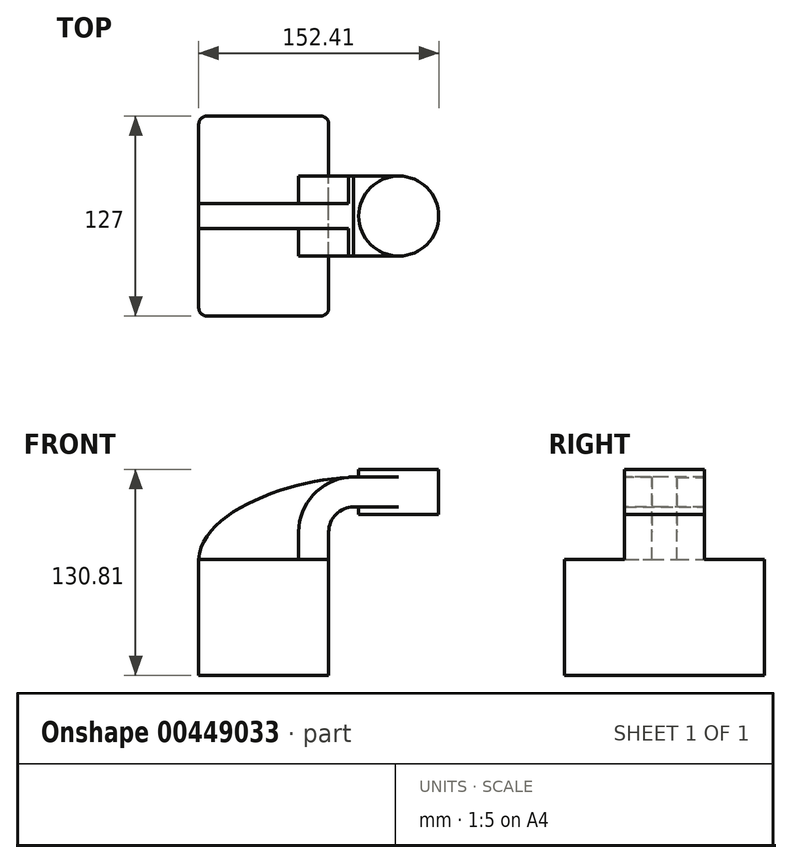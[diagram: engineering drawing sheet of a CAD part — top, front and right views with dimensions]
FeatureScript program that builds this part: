
annotation { "Feature Type Name" : "Feature", "Feature Type Description" : "" }
export const myFeature = defineFeature(function(context is Context, id is Id, definition is map)
    precondition{}
    {
        {
            var Q0;
            Q0=qCreatedBy(makeId("Front.planeOp"),FACE);
            var sketch = newSketch(context, id + "F0", { "sketchPlane" : qUnion([Q0])});
            skLineSegment(sketch, "E0.rect.bottom", {"start": v(-41.28, 9.52) * mm, "end": v(41.28, 9.52) * mm});
            skLineSegment(sketch, "E0.rect.top", {"start": v(-41.28, -9.52) * mm, "end": v(41.28, -9.52) * mm});
            skLineSegment(sketch, "E0.rect.left", {"start": v(-41.28, 9.52) * mm, "end": v(-41.28, -9.52) * mm});
            skLineSegment(sketch, "E0.rect.right", {"start": v(41.28, 9.52) * mm, "end": v(41.28, -9.52) * mm});
            skPoint(sketch, "E0.rect.middle", {"position": v(0, 0) * mm});
            skLineSegment(sketch, "E1", {"start": v(41.28, 9.52) * mm, "end": v(41.28, 27) * mm});
            skArc(sketch, "E2", {"start": v(41.28, 27) * mm, "mid": v(45.92, 38.23) * mm, "end": v(57.15, 42.88) * mm});
            skLineSegment(sketch, "E3", {"start": v(57.15, 42.88) * mm, "end": v(85.72, 42.88) * mm});
            skLineSegment(sketch, "E4.rect.bottom", {"start": v(60.32, 38.1) * mm, "end": v(111.12, 38.1) * mm});
            skLineSegment(sketch, "E4.rect.top", {"start": v(60.32, 66.68) * mm, "end": v(111.12, 66.68) * mm});
            skLineSegment(sketch, "E4.rect.left", {"start": v(60.32, 38.1) * mm, "end": v(60.32, 66.68) * mm});
            skLineSegment(sketch, "E4.rect.right", {"start": v(111.13, 38.1) * mm, "end": v(111.12, 66.68) * mm});
            skPoint(sketch, "E4.rect.middle", {"position": v(85.72, 52.39) * mm});
            skLineSegment(sketch, "E5.0", {"start": v(57.15, 61.93) * mm, "end": v(85.72, 61.93) * mm});
            skArc(sketch, "E5.1", {"start": v(22.23, 27) * mm, "mid": v(32.45, 51.7) * mm, "end": v(57.15, 61.93) * mm});
            skLineSegment(sketch, "E5.2", {"start": v(22.23, 9.52) * mm, "end": v(22.23, 27) * mm});
            skLineSegment(sketch, "E6", {"start": v(85.72, 38.1) * mm, "end": v(85.72, 66.68) * mm});
            skFitSpline(sketch, "E7", {"points": [v(-41.28, 9.53) * mm, v(57.15, 61.93) * mm], "startDerivative": vector(5.2, 92.34) * mm, "endDerivative": vector(120.92, 4.22) * mm});
            skSolve(sketch);
        }
        {
            var Q0;
            Q0=makeQuery(id+"F0.imprint","IMPRINT",FACE,{"disambiguationData":[TD([[makeQuery(id+"F0.imprint","IMPRINT",EDGE,{"derivedFrom":sQuery(id+"F0.wireOp",EDGE,"E0.rect.top")}),1.0]])]});
            extrude(context, id + "F1", {"entities" : qUnion([Q0]), "endBound" : BoundingType.SYMMETRIC, "depth" : 127 * mm});
        }
        {
            var Q0;
            {var subQ9=sQuery(id+"F0.wireOp",EDGE,"E1");Q0=makeQuery(id+"F0.imprint","IMPRINT",FACE,{"disambiguationData":[TD([[makeQuery(id+"F0.imprint","IMPRINT",EDGE,{"derivedFrom":subQ9}),1.0]])]});}
            var Q1;
            {var subQ0=sQuery(id+"F0.wireOp",EDGE,"E6");var subQ1=sQuery(id+"F0.wireOp",EDGE,"E3");var subQ2=makeQuery(id+"F0.imprint","INTERSECT",VERTEX,{"derivedFrom":[subQ1,subQ0]});Q1=makeQuery(id+"F0.imprint","IMPRINT",FACE,{"disambiguationData":[TD([[makeQuery(id+"F0.imprint","IMPRINT",EDGE,{"disambiguationData":[TD([[subQ2,1.0]])],"derivedFrom":subQ1}),1.0]])]});}
            extrude(context, id + "F2", {"entities" : qUnion([Q0, Q1]), "operationType" : NewBodyOperationType.ADD, "endBound" : BoundingType.SYMMETRIC, "depth" : 50.8 * mm});
        }
        {
            var Q0;
            {var subQ3=sQuery(id+"F0.wireOp",EDGE,"E5.2");Q0=makeQuery(id+"F0.imprint","IMPRINT",FACE,{"disambiguationData":[TD([[makeQuery(id+"F0.imprint","IMPRINT",EDGE,{"derivedFrom":subQ3}),1.0]])]});}
            extrude(context, id + "F3", {"entities" : qUnion([Q0]), "operationType" : NewBodyOperationType.ADD, "endBound" : BoundingType.SYMMETRIC, "depth" : 15.88 * mm});
        }
        {
            var Q0;
            {var subQ5=sQuery(id+"F0.wireOp",EDGE,"E4.rect.right");Q0=makeQuery(id+"F0.imprint","IMPRINT",FACE,{"disambiguationData":[TD([[makeQuery(id+"F0.imprint","IMPRINT",EDGE,{"derivedFrom":subQ5}),1.0]])]});}
            var Q1;
            Q1=sQuery(id+"F0.wireOp",EDGE,"E6");
            revolve(context, id + "F4", {"operationType" : NewBodyOperationType.ADD, "entities" : qUnion([Q0]), "axis" : qUnion([Q1]), "revolveType" : RevolveType.FULL});
        }
        {
            var Q0;
            Q0=makeQuery(id+"F1.opExtrude","CAP_EDGE",EDGE,{"disambiguationData":[OSD([sQuery(id+"F0.wireOp",EDGE,"E0.rect.right")])],"isStart":false});
            var Q1;
            Q1=makeQuery(id+"F1.opExtrude","CAP_EDGE",EDGE,{"disambiguationData":[OSD([sQuery(id+"F0.wireOp",EDGE,"E0.rect.left")])],"isStart":false});
            var Q2;
            Q2=makeQuery(id+"F1.opExtrude","CAP_EDGE",EDGE,{"disambiguationData":[OSD([sQuery(id+"F0.wireOp",EDGE,"E0.rect.right")])],"isStart":true});
            var Q3;
            Q3=makeQuery(id+"F1.opExtrude","CAP_EDGE",EDGE,{"disambiguationData":[OSD([sQuery(id+"F0.wireOp",EDGE,"E0.rect.left")])],"isStart":true});
            fillet(context, id + "F5", {"entities" : qUnion([Q0, Q1, Q2, Q3]), "radius" : 5.08 * mm, "tangentPropagation" : true, "allowEdgeOverflow" : false});
        }
        {
            var Q0;
            Q0=makeQuery(id+"F1.opExtrude","SWEPT_FACE",FACE,{"disambiguationData":[OSD([sQuery(id+"F0.wireOp",EDGE,"E0.rect.top")])]});
            extrude(context, id + "F6", {"entities" : qUnion([Q0]), "operationType" : NewBodyOperationType.ADD, "depth" : 54.6 * mm});
        }
    });
